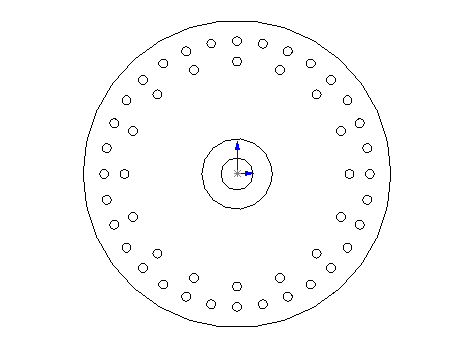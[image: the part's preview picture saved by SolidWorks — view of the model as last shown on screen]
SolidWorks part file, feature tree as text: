
SOLIDWORKS PART (.sldprt)
format: sldprt  version: not decoded by parser v0  size: 172,544 bytes
history: native  units: mm
features: sketch x4, extrude x2, cut_extrude x2, material x1 (+15 scaffold rows collapsed)
feature tree (24):
  scaffold x15  (default folders/planes/origin — collapsed)
  material  "Material <not specified>"
  sketch  "Sketch1"  dims[D1=23.75mm]
  extrude  "Extrude1"  Depth=5mm
  sketch  "Sketch2"  dims[D1=6.35mm]
  extrude  "Extrude2"  Depth=5mm
  sketch  "Sketch3"  dims[D1=1.5875mm]
  cut_extrude  "Cut-Extrude1"  [1 undecoded]
  sketch  "Sketch4"  dims[D1=~1.149337mm]
  cut_extrude  "Cut-Extrude2"  [1 undecoded]
decode coverage: 6 of 8 modeling features carry decoded parameters
note: ~ marks probable driven/reference dimensions
note: 2 parameter values undecoded
note: suppression state not decoded; provenance and decode notes live in map.json
